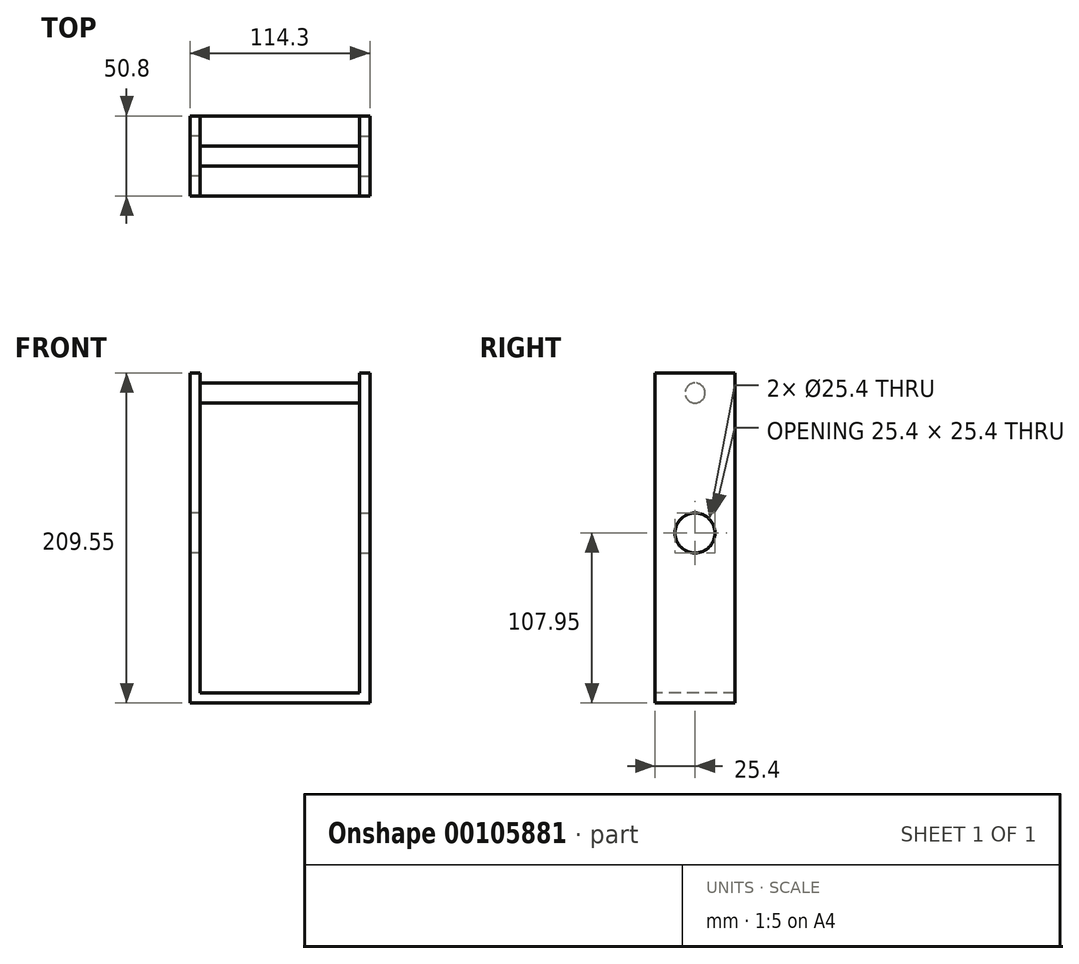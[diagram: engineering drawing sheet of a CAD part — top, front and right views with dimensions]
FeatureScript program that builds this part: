
annotation { "Feature Type Name" : "Feature", "Feature Type Description" : "" }
export const myFeature = defineFeature(function(context is Context, id is Id, definition is map)
    precondition{}
    {
        {
            var Q0;
            Q0=qCreatedBy(makeId("Top.planeOp"),FACE);
            var sketch = newSketch(context, id + "F0", { "sketchPlane" : qUnion([Q0])});
            skLineSegment(sketch, "E0.bottom", {"start": v(0, 25.4) * mm, "end": v(-57.15, 25.4) * mm});
            skLineSegment(sketch, "E0.top", {"start": v(0, -25.4) * mm, "end": v(-57.15, -25.4) * mm});
            skLineSegment(sketch, "E0.right", {"start": v(-57.15, 25.4) * mm, "end": v(-57.15, -25.4) * mm});
            skPoint(sketch, "E0.middle", {"position": v(0, 0) * mm});
            skLineSegment(sketch, "E1", {"start": v(0, 25.4) * mm, "end": v(0, -25.4) * mm});
            skSolve(sketch);
        }
        {
            var Q0;
            Q0=qSketchRegion(id+"F0",true);
            extrude(context, id + "F1", {"entities" : qUnion([Q0]), "depth" : 6.35 * mm});
        }
        {
            var Q0;
            Q0=makeQuery(id+"F1.opExtrude","CAP_FACE",FACE,{"disambiguationData":[OSD([sQuery(id+"F0.wireOp",EDGE,"E0.bottom"),sQuery(id+"F0.wireOp",EDGE,"E0.top"),sQuery(id+"F0.wireOp",EDGE,"E0.left"),sQuery(id+"F0.wireOp",EDGE,"E0.right")])],"isStart":false});
            var sketch = newSketch(context, id + "F2", { "sketchPlane" : qUnion([Q0])});
            skLineSegment(sketch, "E2.bottom", {"start": v(-57.15, 25.4) * mm, "end": v(-50.8, 25.4) * mm});
            skLineSegment(sketch, "E2.top", {"start": v(-57.15, -25.4) * mm, "end": v(-50.8, -25.4) * mm});
            skLineSegment(sketch, "E2.left", {"start": v(-57.15, 25.4) * mm, "end": v(-57.15, -25.4) * mm});
            skLineSegment(sketch, "E2.right", {"start": v(-50.8, 25.4) * mm, "end": v(-50.8, -25.4) * mm});
            skSolve(sketch);
        }
        {
            var Q0;
            Q0=qSketchRegion(id+"F2",true);
            extrude(context, id + "F3", {"entities" : qUnion([Q0]), "operationType" : NewBodyOperationType.ADD, "depth" : 203.2 * mm});
        }
        {
            var Q0;
            Q0=makeQuery(id+"F3.boolean.opBoolean","MERGE",FACE,{"derivedFrom":[makeQuery(id+"F1.opExtrude","SWEPT_FACE",FACE,{"disambiguationData":[OSD([sQuery(id+"F0.wireOp",EDGE,"E0.right")])]}),makeQuery(id+"F3.opExtrude","SWEPT_FACE",FACE,{"disambiguationData":[OSD([sQuery(id+"F2.wireOp",EDGE,"E2.left")])]})]});
            var sketch = newSketch(context, id + "F4", { "sketchPlane" : qUnion([Q0])});
            skCircle(sketch, "E3", {"center": v(0, 107.95) * mm, "radius": 12.7 * mm});
            skSolve(sketch);
        }
        {
            var Q0;
            Q0=qSketchRegion(id+"F4",true);
            extrude(context, id + "F5", {"entities" : qUnion([Q0]), "operationType" : NewBodyOperationType.REMOVE, "endBound" : BoundingType.UP_TO_NEXT, "oppositeDirection" : true, "depth" : 25.4 * mm});
        }
        {
            var Q0;
            Q0=makeQuery(id+"F1.opExtrude","SWEPT_BODY",BODY,{"disambiguationData":[OSD([sQuery(id+"F0.wireOp",EDGE,"E0.bottom"),sQuery(id+"F0.wireOp",EDGE,"E0.top"),sQuery(id+"F0.wireOp",EDGE,"E0.right"),sQuery(id+"F0.wireOp",EDGE,"E1")])]});
            var Q1;
            Q1=qCreatedBy(makeId("Right.planeOp"),FACE);
            mirror(context, id + "F6", {"operationType" : NewBodyOperationType.ADD, "entities" : qUnion([Q0]), "mirrorPlane" : qUnion([Q1])});
        }
        {
            var Q0;
            Q0=makeQuery(id+"F3.opExtrude","SWEPT_FACE",FACE,{"disambiguationData":[OSD([sQuery(id+"F2.wireOp",EDGE,"E2.right")])]});
            var sketch = newSketch(context, id + "F7", { "sketchPlane" : qUnion([Q0])});
            skCircle(sketch, "E4", {"center": v(0, 196.85) * mm, "radius": 6.35 * mm});
            skSolve(sketch);
        }
        {
            var Q0;
            Q0 = qSketchRegion(id + "F7", true);
            var Q1;
            Q1=makeQuery(id+"F6.opPattern","COPY",FACE,{"derivedFrom":makeQuery(id+"F3.opExtrude","SWEPT_FACE",FACE,{"disambiguationData":[OSD([sQuery(id+"F2.wireOp",EDGE,"E2.right")])]}),"instanceName":"1"});
            extrude(context, id + "F8", {"entities" : qUnion([Q0]), "operationType" : NewBodyOperationType.ADD, "endBound" : BoundingType.UP_TO_SURFACE, "endBoundEntityFace" : qUnion([Q1]), "depth" : 25.4 * mm});
        }
    });
